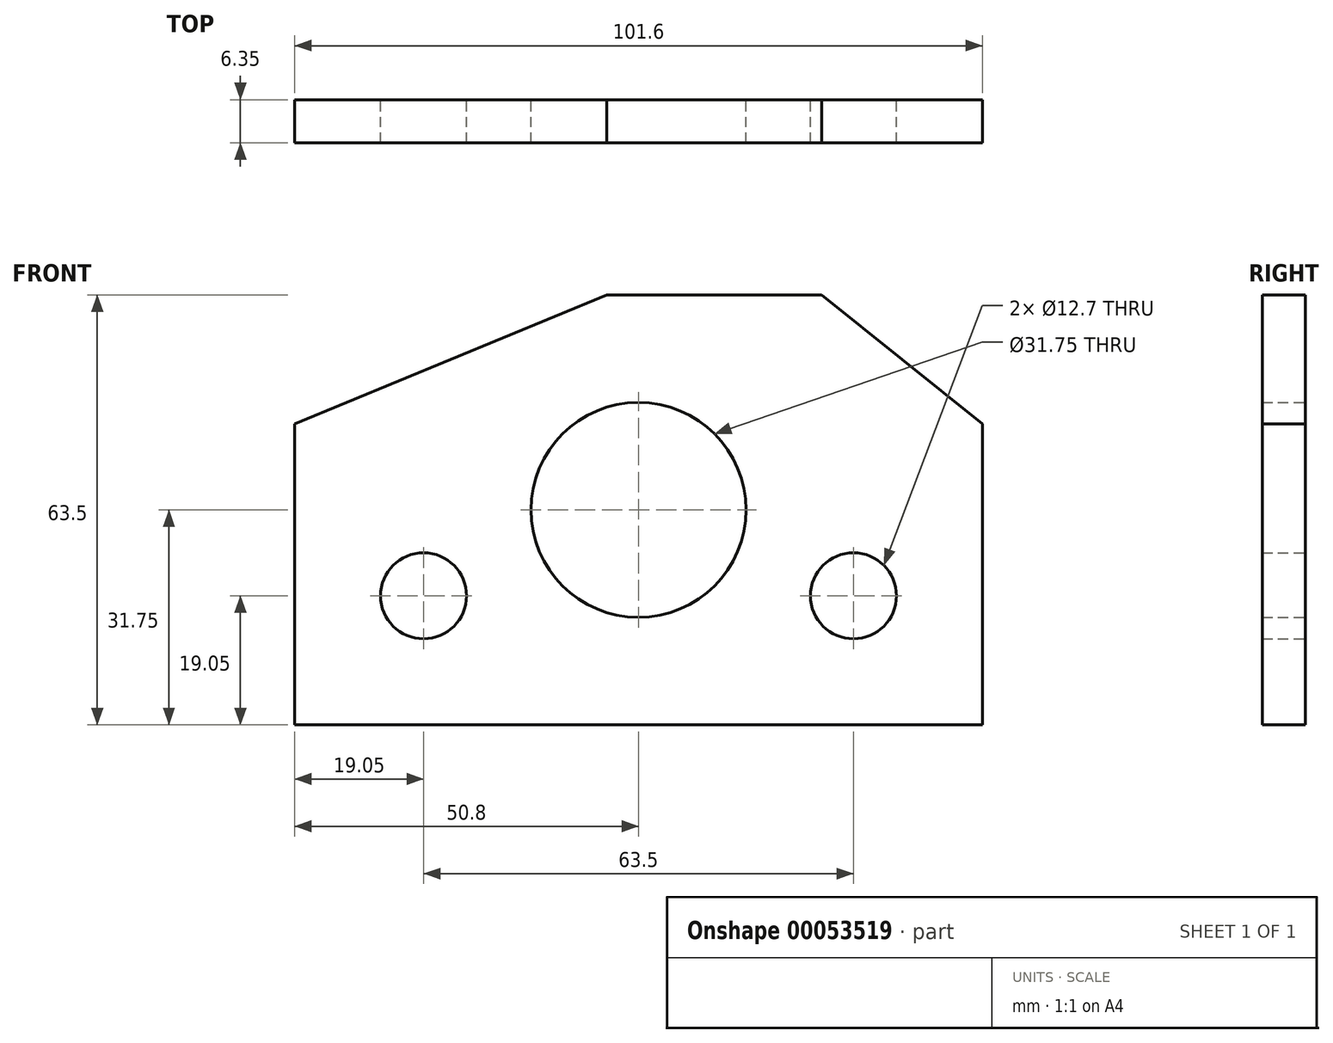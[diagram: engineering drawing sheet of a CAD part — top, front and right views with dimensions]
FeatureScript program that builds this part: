
annotation { "Feature Type Name" : "Feature", "Feature Type Description" : "" }
export const myFeature = defineFeature(function(context is Context, id is Id, definition is map)
    precondition{}
    {
        {
            var Q0;
            Q0=qCreatedBy(makeId("Front.planeOp"),FACE);
            var sketch = newSketch(context, id + "F0", { "sketchPlane" : qUnion([Q0])});
            skCircle(sketch, "E0", {"center": v(0, 0) * mm, "radius": 15.88 * mm});
            skLineSegment(sketch, "E1", {"start": v(-4.68, 31.75) * mm, "end": v(27.07, 31.75) * mm});
            skLineSegment(sketch, "E2", {"start": v(27.07, 31.75) * mm, "end": v(50.8, 12.7) * mm});
            skLineSegment(sketch, "E3", {"start": v(-4.68, 31.75) * mm, "end": v(-50.8, 12.7) * mm});
            skLineSegment(sketch, "E4", {"start": v(-50.8, 12.7) * mm, "end": v(-50.8, -31.75) * mm});
            skLineSegment(sketch, "E5", {"start": v(-50.8, -31.75) * mm, "end": v(50.8, -31.75) * mm});
            skLineSegment(sketch, "E6", {"start": v(50.8, -31.75) * mm, "end": v(50.8, 12.7) * mm});
            skCircle(sketch, "E7", {"center": v(-31.75, -12.7) * mm, "radius": 6.35 * mm});
            skCircle(sketch, "E8", {"center": v(31.75, -12.7) * mm, "radius": 6.35 * mm});
            skSolve(sketch);
        }
        {
            var Q0;
            Q0 = qSketchRegion(id + "F0", true);
            extrude(context, id + "F1", {"entities" : qUnion([Q0]), "depth" : 6.35 * mm});
        }
    });
